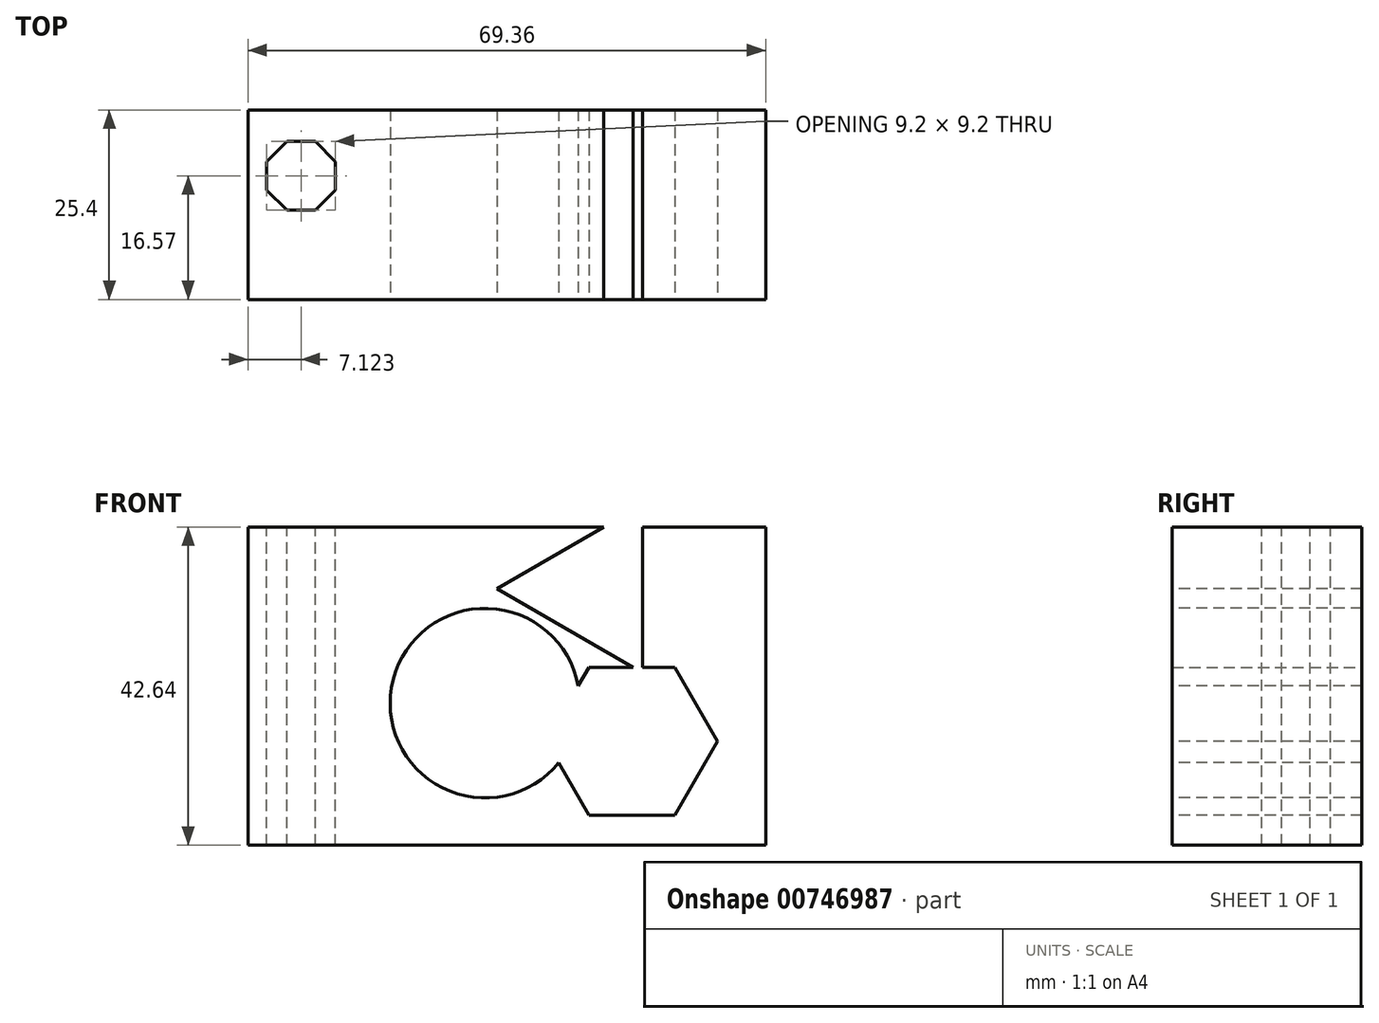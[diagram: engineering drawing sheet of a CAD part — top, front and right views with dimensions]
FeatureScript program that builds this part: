
annotation { "Feature Type Name" : "Feature", "Feature Type Description" : "" }
export const myFeature = defineFeature(function(context is Context, id is Id, definition is map)
    precondition{}
    {
        {
            var Q0;
            Q0=qCreatedBy(makeId("Front.planeOp"),FACE);
            var sketch = newSketch(context, id + "F0", { "sketchPlane" : qUnion([Q0])});
            skLineSegment(sketch, "E0.bottom", {"start": v(0, 0) * mm, "end": v(69.36, 0) * mm});
            skLineSegment(sketch, "E0.top", {"start": v(0, 42.64) * mm, "end": v(69.36, 42.64) * mm});
            skLineSegment(sketch, "E0.left", {"start": v(0, 0) * mm, "end": v(0, 42.64) * mm});
            skLineSegment(sketch, "E0.right", {"start": v(69.36, 0) * mm, "end": v(69.36, 42.64) * mm});
            skSolve(sketch);
        }
        {
            var Q0;
            Q0=makeQuery(id+"F0.imprint","IMPRINT",FACE,{"disambiguationData":[TD([[makeQuery(id+"F0.imprint","IMPRINT",EDGE,{"derivedFrom":sQuery(id+"F0.wireOp",EDGE,"E0.bottom")}),1.0]])]});
            extrude(context, id + "F1", {"entities" : qUnion([Q0]), "depth" : 25.4 * mm, "offsetDistance" : 25.4 * mm});
        }
        {
            var Q0;
            Q0=makeQuery(id+"F1.opExtrude","CAP_FACE",FACE,{"disambiguationData":[OSD([sQuery(id+"F0.wireOp",EDGE,"E0.bottom"),sQuery(id+"F0.wireOp",EDGE,"E0.top"),sQuery(id+"F0.wireOp",EDGE,"E0.left"),sQuery(id+"F0.wireOp",EDGE,"E0.right")])],"isStart":false});
            var sketch = newSketch(context, id + "F2", { "sketchPlane" : qUnion([Q0])});
            skCircle(sketch, "E1", {"center": v(31.75, 19.05) * mm, "radius": 12.7 * mm});
            skCircle(sketch, "E2.cCircle", {"center": v(46.37, 34.4) * mm, "radius": 6.5 * mm, "construction": true});
            skLineSegment(sketch, "E2.0", {"start": v(52.87, 45.65) * mm, "end": v(52.87, 23.14) * mm});
            skLineSegment(sketch, "E2.1", {"start": v(52.87, 23.14) * mm, "end": v(33.38, 34.4) * mm});
            skLineSegment(sketch, "E2.2", {"start": v(33.38, 34.4) * mm, "end": v(52.87, 45.65) * mm});
            skPoint(sketch, "E2.0.midPoint", {"position": v(52.87, 34.4) * mm});
            skSolve(sketch);
        }
        {
            var Q0;
            Q0 = qSketchRegion(id + "F2", true);
            extrude(context, id + "F3", {"entities" : qUnion([Q0]), "operationType" : NewBodyOperationType.REMOVE, "endBound" : BoundingType.THROUGH_ALL, "oppositeDirection" : true, "depth" : 25.4 * mm, "offsetDistance" : 25.4 * mm});
        }
        {
            var Q0;
            Q0 = qSketchRegion(id + "F2", true);
            extrude(context, id + "F4", {"entities" : qUnion([Q0]), "operationType" : NewBodyOperationType.REMOVE, "oppositeDirection" : true, "depth" : 19.05 * mm, "offsetDistance" : 25.4 * mm});
        }
        {
            var Q0;
            Q0=makeQuery(id+"F1.opExtrude","CAP_FACE",FACE,{"disambiguationData":[OSD([sQuery(id+"F0.wireOp",EDGE,"E0.bottom"),sQuery(id+"F0.wireOp",EDGE,"E0.top"),sQuery(id+"F0.wireOp",EDGE,"E0.left"),sQuery(id+"F0.wireOp",EDGE,"E0.right")])],"isStart":false});
            var sketch = newSketch(context, id + "F5", { "sketchPlane" : qUnion([Q0])});
            skCircle(sketch, "E3.cCircle", {"center": v(51.44, 13.94) * mm, "radius": 9.93 * mm, "construction": true});
            skLineSegment(sketch, "E3.0", {"start": v(57.17, 4) * mm, "end": v(45.7, 4) * mm});
            skLineSegment(sketch, "E3.1", {"start": v(45.7, 4) * mm, "end": v(39.97, 13.94) * mm});
            skLineSegment(sketch, "E3.2", {"start": v(39.97, 13.94) * mm, "end": v(45.7, 23.87) * mm});
            skLineSegment(sketch, "E3.3", {"start": v(45.7, 23.87) * mm, "end": v(57.17, 23.87) * mm});
            skLineSegment(sketch, "E3.4", {"start": v(57.17, 23.87) * mm, "end": v(62.9, 13.94) * mm});
            skLineSegment(sketch, "E3.5", {"start": v(62.9, 13.94) * mm, "end": v(57.17, 4) * mm});
            skPoint(sketch, "E3.0.midPoint", {"position": v(51.44, 4) * mm});
            skSolve(sketch);
        }
        {
            var Q0;
            Q0 = qSketchRegion(id + "F5", true);
            extrude(context, id + "F6", {"entities" : qUnion([Q0]), "operationType" : NewBodyOperationType.REMOVE, "oppositeDirection" : true, "depth" : 25.4 * mm, "offsetDistance" : 25.4 * mm});
        }
        {
            var Q0;
            {var subQ1=sQuery(id+"F0.wireOp",EDGE,"E0.left");var subQ2=sQuery(id+"F0.wireOp",EDGE,"E0.top");Q0=makeQuery(id+"F3.boolean.opBoolean","SPLIT",FACE,{"disambiguationData":[TD([makeQuery(id+"F1.opExtrude","SWEPT_FACE",FACE,{"disambiguationData":[OSD([subQ1])]})])],"derivedFrom":makeQuery(id+"F1.opExtrude","SWEPT_FACE",FACE,{"disambiguationData":[OSD([subQ2])]})});}
            var sketch = newSketch(context, id + "F7", { "sketchPlane" : qUnion([Q0])});
            skCircle(sketch, "E4.cCircle", {"center": v(7.12, -8.83) * mm, "radius": 4.6 * mm, "construction": true});
            skLineSegment(sketch, "E4.0", {"start": v(9.03, -13.43) * mm, "end": v(5.22, -13.43) * mm});
            skLineSegment(sketch, "E4.1", {"start": v(5.22, -13.43) * mm, "end": v(2.52, -10.74) * mm});
            skLineSegment(sketch, "E4.2", {"start": v(2.52, -10.74) * mm, "end": v(2.52, -6.92) * mm});
            skLineSegment(sketch, "E4.3", {"start": v(2.52, -6.92) * mm, "end": v(5.22, -4.23) * mm});
            skLineSegment(sketch, "E4.4", {"start": v(5.22, -4.23) * mm, "end": v(9.03, -4.23) * mm});
            skLineSegment(sketch, "E4.5", {"start": v(9.03, -4.23) * mm, "end": v(11.72, -6.92) * mm});
            skLineSegment(sketch, "E4.6", {"start": v(11.72, -6.92) * mm, "end": v(11.72, -10.74) * mm});
            skLineSegment(sketch, "E4.7", {"start": v(11.72, -10.74) * mm, "end": v(9.03, -13.43) * mm});
            skPoint(sketch, "E4.0.midPoint", {"position": v(7.12, -13.43) * mm});
            skSolve(sketch);
        }
        {
            var Q0;
            Q0 = qSketchRegion(id + "F7", true);
            extrude(context, id + "F8", {"entities" : qUnion([Q0]), "operationType" : NewBodyOperationType.REMOVE, "endBound" : BoundingType.THROUGH_ALL, "oppositeDirection" : true, "depth" : 25.4 * mm, "offsetDistance" : 25.4 * mm});
        }
    });
